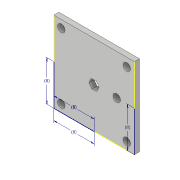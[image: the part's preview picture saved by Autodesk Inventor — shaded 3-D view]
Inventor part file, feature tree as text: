
AUTODESK INVENTOR PART (.ipt)
format: ipt  version: 2019 (Build 230136000, 136)  size: 130,048 bytes
history: native  units: in
note: dims shown in document units (in); Inventor stores cm internally (conversion verified against a paired STEP export)
features: sketch x7, extrude x4
ambient origin geometry x8: Origin, YZ Plane, XZ Plane, XY Plane, X Axis, Y Axis, Z Axis, Center Point
bodies: Solid1 (feature_tree)
feature tree (11):
  extrude  "Extrusion1"  Depth=6.2992in
  extrude  "Extrusion2"  Depth=0.3937in
  sketch  "Sketch3"  dims[d5=0.5906in d6=0.5906in]
  sketch  "Sketch4"  dims[d7=0.5906in d8=0.5906in]
  extrude  "Extrusion3"  Depth=0.5906in
  sketch  "Sketch6"  dims[d10=0.5906in]
  extrude  "Extrusion4"  Depth=0.5906in
  sketch  "Sketch1"  dims[d0=6.2992in d1=6.2992in]
  sketch  "Sketch2"  dims[d2=0.3937in d3=0.0in d4=0.5906in]
  sketch  "Sketch5"  dims[d9=0.6496in]
  sketch  "Sketch7"  dims[d11=0.5906in d12=0.5906in d13=0.5906in d14=0.5906in d15=0.5906in d16=0.3937in d17=0.0in d18=3.1496in d19=3.1496in d20=3.1496in d21=3.1496in d22=3.1496in d23=0.3937in d24=0.3937in d25=0.0in d26=3.1496in d27=1.378in d28=0.5906in d29=0.3937in d30=0.0in]
